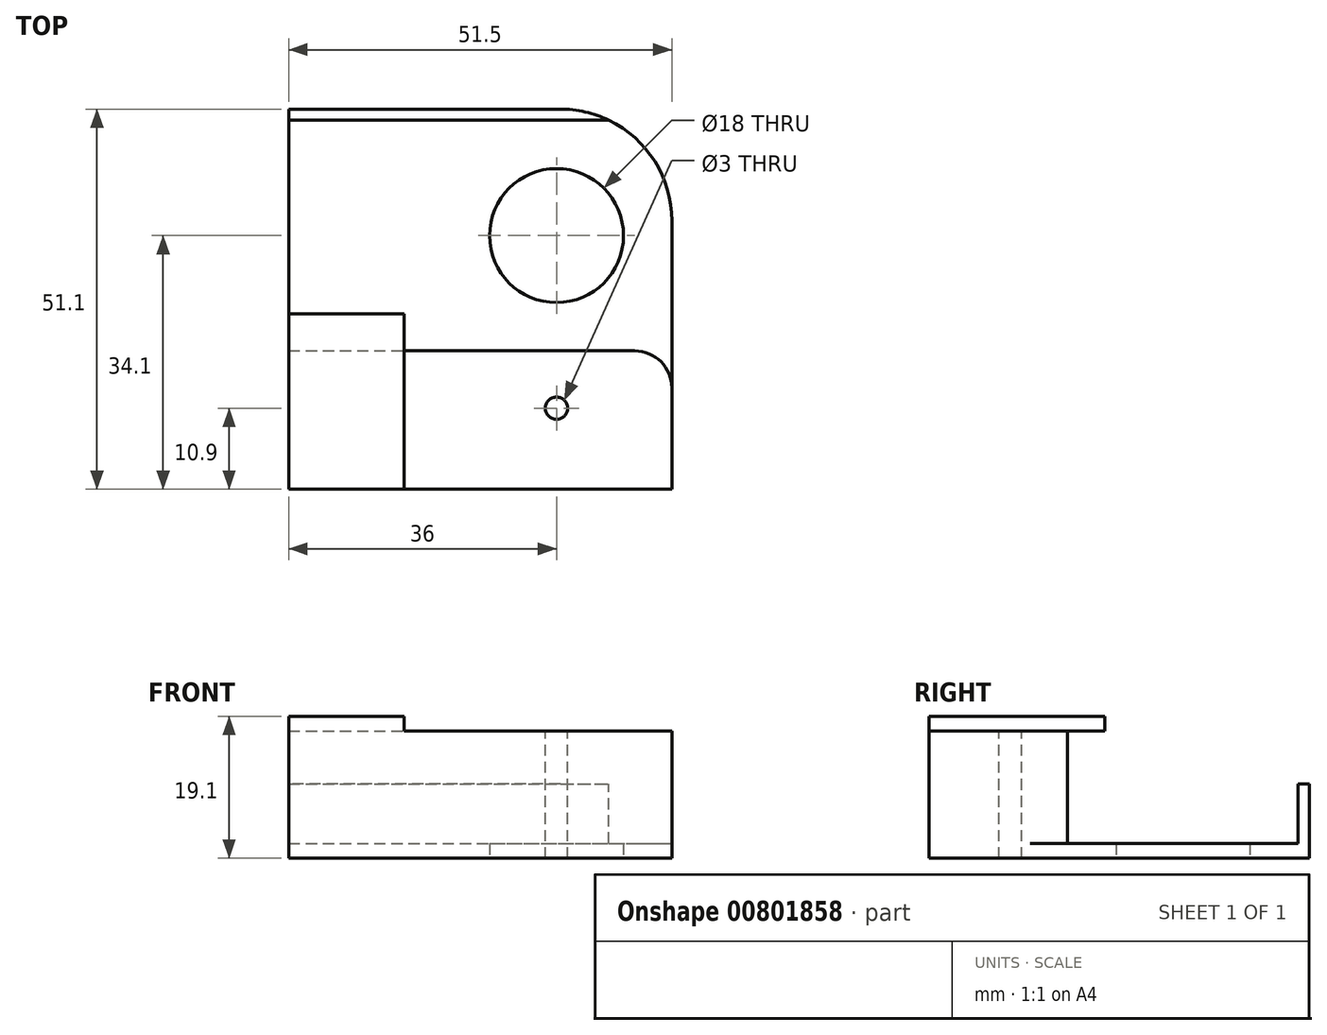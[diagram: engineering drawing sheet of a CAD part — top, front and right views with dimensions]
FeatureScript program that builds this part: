
annotation { "Feature Type Name" : "Feature", "Feature Type Description" : "" }
export const myFeature = defineFeature(function(context is Context, id is Id, definition is map)
    precondition{}
    {
        {
            var Q0;
            Q0=qCreatedBy(makeId("Top.planeOp"),FACE);
            var sketch = newSketch(context, id + "F0", { "sketchPlane" : qUnion([Q0])});
            skCircle(sketch, "E0", {"center": v(0, 0) * mm, "radius": 9 * mm});
            skLineSegment(sketch, "E1.bottom", {"start": v(15.5, -15.5) * mm, "end": v(-15.5, -15.5) * mm});
            skLineSegment(sketch, "E1.top", {"start": v(15.5, 15.5) * mm, "end": v(-15.5, 15.5) * mm});
            skLineSegment(sketch, "E1.left", {"start": v(15.5, -15.5) * mm, "end": v(15.5, 15.5) * mm});
            skLineSegment(sketch, "E1.right", {"start": v(-15.5, -15.5) * mm, "end": v(-15.5, 15.5) * mm});
            skLineSegment(sketch, "E2.bottom", {"start": v(15.5, 15.5) * mm, "end": v(36, 15.5) * mm});
            skLineSegment(sketch, "E2.top", {"start": v(15.5, -15.5) * mm, "end": v(36, -15.5) * mm});
            skLineSegment(sketch, "E2.left", {"start": v(15.5, 15.5) * mm, "end": v(15.5, -15.5) * mm});
            skLineSegment(sketch, "E2.right", {"start": v(36, 15.5) * mm, "end": v(36, -15.5) * mm});
            skLineSegment(sketch, "E3.bottom", {"start": v(-15.5, -15.5) * mm, "end": v(36, -15.5) * mm});
            skLineSegment(sketch, "E3.top", {"start": v(-15.5, -34.1) * mm, "end": v(36, -34.1) * mm});
            skLineSegment(sketch, "E3.left", {"start": v(-15.5, -15.5) * mm, "end": v(-15.5, -34.1) * mm});
            skLineSegment(sketch, "E3.right", {"start": v(36, -15.5) * mm, "end": v(36, -34.1) * mm});
            skLineSegment(sketch, "E4.bottom", {"start": v(-15.5, 15.5) * mm, "end": v(36, 15.5) * mm});
            skLineSegment(sketch, "E4.top", {"start": v(-15.5, 17) * mm, "end": v(36, 17) * mm});
            skLineSegment(sketch, "E4.left", {"start": v(-15.5, 15.5) * mm, "end": v(-15.5, 17) * mm});
            skLineSegment(sketch, "E4.right", {"start": v(36, 15.5) * mm, "end": v(36, 17) * mm});
            skSolve(sketch);
        }
        {
            var Q0;
            Q0=makeQuery(id+"F0.imprint","IMPRINT",FACE,{"disambiguationData":[TD([[makeQuery(id+"F0.imprint","IMPRINT",EDGE,{"derivedFrom":sQuery(id+"F0.wireOp",EDGE,"E1.bottom")}),1.0]])]});
            extrude(context, id + "F1", {"entities" : qUnion([Q0]), "depth" : 17.1 * mm, "offsetDistance" : 25 * mm});
        }
        {
            var Q0;
            Q0=makeQuery(id+"F0.imprint","IMPRINT",FACE,{"disambiguationData":[TD([[makeQuery(id+"F0.imprint","IMPRINT",EDGE,{"derivedFrom":sQuery(id+"F0.wireOp",EDGE,"E0")}),-1.0]])]});
            var Q1;
            Q1=makeQuery(id+"F0.imprint","IMPRINT",FACE,{"disambiguationData":[TD([[makeQuery(id+"F0.imprint","IMPRINT",EDGE,{"derivedFrom":sQuery(id+"F0.wireOp",EDGE,"E1.left")}),-1.0]])]});
            extrude(context, id + "F2", {"entities" : qUnion([Q0, Q1]), "operationType" : NewBodyOperationType.ADD, "depth" : 2 * mm, "offsetDistance" : 25 * mm});
        }
        {
            var Q0;
            Q0=makeQuery(id+"F0.imprint","IMPRINT",FACE,{"disambiguationData":[TD([[makeQuery(id+"F0.imprint","IMPRINT",EDGE,{"derivedFrom":sQuery(id+"F0.wireOp",EDGE,"E1.top")}),-1.0]])]});
            extrude(context, id + "F3", {"entities" : qUnion([Q0]), "operationType" : NewBodyOperationType.ADD, "depth" : 10 * mm, "offsetDistance" : 25 * mm});
        }
        {
            var Q0;
            Q0=makeQuery(id+"F3.opExtrude","SWEPT_EDGE",EDGE,{"disambiguationData":[OSD([sQuery(id+"F0.wireOp",EDGE,"E4.top"),sQuery(id+"F0.wireOp",EDGE,"E4.left")])]});
            fillet(context, id + "F4", {"entities" : qUnion([Q0]), "radius" : 15 * mm, "tangentPropagation" : true, "allowEdgeOverflow" : false});
        }
        {
            var Q0;
            Q0=makeQuery(id+"F1.opExtrude","CAP_FACE",FACE,{"disambiguationData":[OSD([sQuery(id+"F0.wireOp",EDGE,"E1.bottom"),sQuery(id+"F0.wireOp",EDGE,"E2.top"),sQuery(id+"F0.wireOp",EDGE,"E3.top"),sQuery(id+"F0.wireOp",EDGE,"E3.left"),sQuery(id+"F0.wireOp",EDGE,"E3.right")])],"isStart":false});
            var sketch = newSketch(context, id + "F5", { "sketchPlane" : qUnion([Q0])});
            skLineSegment(sketch, "E5.bottom", {"start": v(36, -34.1) * mm, "end": v(20.5, -34.1) * mm});
            skLineSegment(sketch, "E5.top", {"start": v(36, -10.5) * mm, "end": v(20.5, -10.5) * mm});
            skLineSegment(sketch, "E5.left", {"start": v(36, -34.1) * mm, "end": v(36, -10.5) * mm});
            skLineSegment(sketch, "E5.right", {"start": v(20.5, -34.1) * mm, "end": v(20.5, -10.5) * mm});
            skPoint(sketch, "E6", {"position": v(0, -23.2) * mm});
            skSolve(sketch);
        }
        {
            var Q0;
            {var subQ0=sQuery(id+"F5.wireOp",EDGE,"E5.top");Q0=makeQuery(id+"F5.imprint","IMPRINT",FACE,{"disambiguationData":[TD([[makeQuery(id+"F5.imprint","IMPRINT",EDGE,{"derivedFrom":subQ0}),1.0]])]});}
            var Q1;
            {var subQ0=sQuery(id+"F5.wireOp",EDGE,"E5.bottom");Q1=makeQuery(id+"F5.imprint","IMPRINT",FACE,{"disambiguationData":[TD([[makeQuery(id+"F5.imprint","IMPRINT",EDGE,{"derivedFrom":subQ0}),1.0]])]});}
            extrude(context, id + "F6", {"entities" : qUnion([Q0, Q1]), "operationType" : NewBodyOperationType.ADD, "depth" : 2 * mm, "offsetDistance" : 25 * mm});
        }
        {
            var Q0;
            Q0=sQuery(id+"F5.wireOp",VERTEX,"E6");
            var Q1;
            Q1=makeQuery(id+"F1.opExtrude","SWEPT_BODY",BODY,{"disambiguationData":[OSD([sQuery(id+"F0.wireOp",EDGE,"E1.bottom"),sQuery(id+"F0.wireOp",EDGE,"E2.top"),sQuery(id+"F0.wireOp",EDGE,"E3.top"),sQuery(id+"F0.wireOp",EDGE,"E3.left"),sQuery(id+"F0.wireOp",EDGE,"E3.right")])]});
            hole(context, id + "F7", {"style" : HoleStyle.SIMPLE, "endStyle" : HoleEndStyle.THROUGH, "holeDiameter" : 3 * mm, "majorDiameter" : 5 * mm, "isTappedThrough" : true, "tappedDepth" : 12 * mm, "tapClearance" : 3, "locations" : qUnion([Q0]), "scope" : qUnion([Q1])});
        }
        {
            var Q0;
            Q0=makeQuery(id+"F1.opExtrude","SWEPT_EDGE",EDGE,{"disambiguationData":[OSD([sQuery(id+"F0.wireOp",EDGE,"E1.bottom"),sQuery(id+"F0.wireOp",EDGE,"E1.right"),sQuery(id+"F0.wireOp",EDGE,"E3.left")])]});
            fillet(context, id + "F8", {"entities" : qUnion([Q0]), "radius" : 5 * mm, "tangentPropagation" : true, "allowEdgeOverflow" : false});
        }
        {
            var Q0;
            Q0=makeQuery(id+"F1.opExtrude","SWEPT_BODY",BODY,{"disambiguationData":[OSD([sQuery(id+"F0.wireOp",EDGE,"E1.bottom"),sQuery(id+"F0.wireOp",EDGE,"E2.top"),sQuery(id+"F0.wireOp",EDGE,"E3.top"),sQuery(id+"F0.wireOp",EDGE,"E3.left"),sQuery(id+"F0.wireOp",EDGE,"E3.right")])]});
            var Q1;
            Q1=makeQuery(id+"F6.boolean.opBoolean","MERGE",FACE,{"derivedFrom":[makeQuery(id+"F3.boolean.opBoolean","MERGE",FACE,{"derivedFrom":[makeQuery(id+"F2.boolean.opBoolean","MERGE",FACE,{"derivedFrom":[makeQuery(id+"F1.opExtrude","SWEPT_FACE",FACE,{"disambiguationData":[OSD([sQuery(id+"F0.wireOp",EDGE,"E3.right")])]}),makeQuery(id+"F2.opExtrude","SWEPT_FACE",FACE,{"disambiguationData":[OSD([sQuery(id+"F0.wireOp",EDGE,"E2.right")])]})]}),makeQuery(id+"F3.opExtrude","SWEPT_FACE",FACE,{"disambiguationData":[OSD([sQuery(id+"F0.wireOp",EDGE,"E4.right")])]})]}),makeQuery(id+"F6.opExtrude","SWEPT_FACE",FACE,{"disambiguationData":[OSD([sQuery(id+"F5.wireOp",EDGE,"E5.left")])]})]});
            mirror(context, id + "F9", {"entities" : qUnion([Q0]), "mirrorPlane" : qUnion([Q1])});
        }
        {
            var Q0;
            Q0=makeQuery(id+"F1.opExtrude","SWEPT_BODY",BODY,{"disambiguationData":[OSD([sQuery(id+"F0.wireOp",EDGE,"E1.bottom"),sQuery(id+"F0.wireOp",EDGE,"E2.top"),sQuery(id+"F0.wireOp",EDGE,"E3.top"),sQuery(id+"F0.wireOp",EDGE,"E3.left"),sQuery(id+"F0.wireOp",EDGE,"E3.right")])]});
            deleteBodies(context, id + "F10", {"entities" : qUnion([Q0])});
        }
    });
